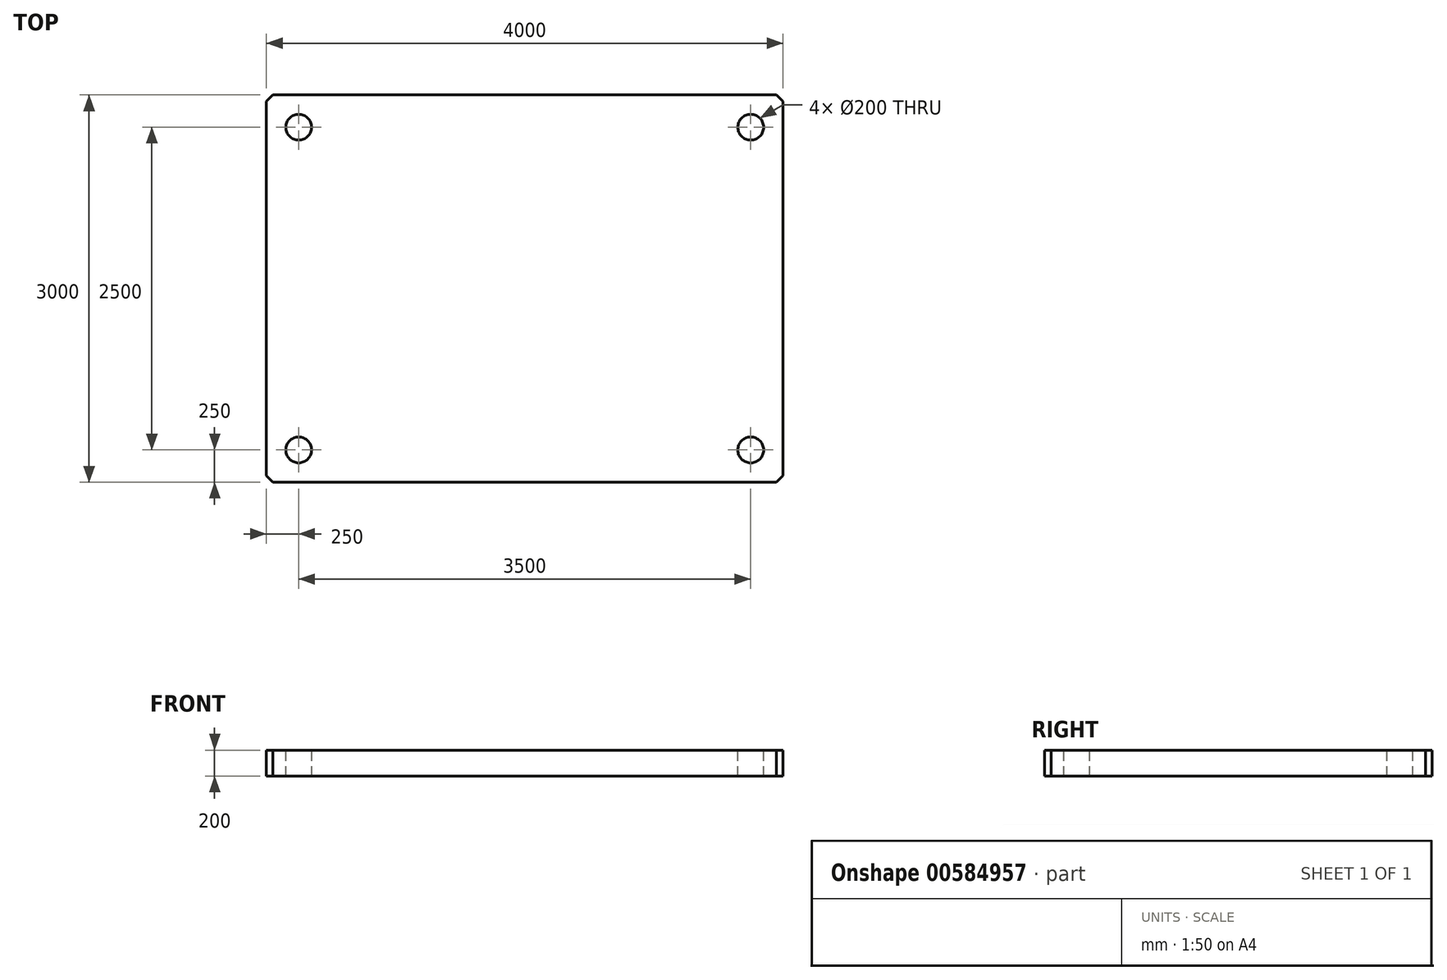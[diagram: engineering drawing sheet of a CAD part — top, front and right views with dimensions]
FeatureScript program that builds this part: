
annotation { "Feature Type Name" : "Feature", "Feature Type Description" : "" }
export const myFeature = defineFeature(function(context is Context, id is Id, definition is map)
    precondition{}
    {
        {
            var Q0;
            Q0=qCreatedBy(makeId("Top.planeOp"),FACE);
            var sketch = newSketch(context, id + "F0", { "sketchPlane" : qUnion([Q0])});
            skLineSegment(sketch, "E0.bottom", {"start": v(2000, -1500) * mm, "end": v(-2000, -1500) * mm});
            skLineSegment(sketch, "E0.top", {"start": v(2000, 1500) * mm, "end": v(-2000, 1500) * mm});
            skLineSegment(sketch, "E0.left", {"start": v(2000, -1500) * mm, "end": v(2000, 1500) * mm});
            skLineSegment(sketch, "E0.right", {"start": v(-2000, -1500) * mm, "end": v(-2000, 1500) * mm});
            skPoint(sketch, "E0.middle", {"position": v(0, 0) * mm});
            skSolve(sketch);
        }
        {
            var Q0;
            Q0 = qSketchRegion(id + "F0", true);
            extrude(context, id + "F1", {"entities" : qUnion([Q0]), "oppositeDirection" : true, "depth" : 200 * mm, "offsetDistance" : 25 * mm, "symmetric" : true});
        }
        {
            var Q0;
            Q0=makeQuery(id+"F1.opExtrude","SWEPT_EDGE",EDGE,{"disambiguationData":[OSD([sQuery(id+"F0.wireOp",EDGE,"E0.bottom"),sQuery(id+"F0.wireOp",EDGE,"E0.right")])]});
            var Q1;
            Q1=makeQuery(id+"F1.opExtrude","SWEPT_EDGE",EDGE,{"disambiguationData":[OSD([sQuery(id+"F0.wireOp",EDGE,"E0.top"),sQuery(id+"F0.wireOp",EDGE,"E0.left")])]});
            var Q2;
            Q2=makeQuery(id+"F1.opExtrude","SWEPT_EDGE",EDGE,{"disambiguationData":[OSD([sQuery(id+"F0.wireOp",EDGE,"E0.bottom"),sQuery(id+"F0.wireOp",EDGE,"E0.left")])]});
            var Q3;
            Q3=makeQuery(id+"F1.opExtrude","SWEPT_EDGE",EDGE,{"disambiguationData":[OSD([sQuery(id+"F0.wireOp",EDGE,"E0.top"),sQuery(id+"F0.wireOp",EDGE,"E0.right")])]});
            chamfer(context, id + "F2", {"entities" : qUnion([Q0, Q1, Q2, Q3]), "width" : 50 * mm, "tangentPropagation" : true});
        }
        {
            var Q0;
            Q0=makeQuery(id+"F1.opExtrude","CAP_FACE",FACE,{"disambiguationData":[OSD([sQuery(id+"F0.wireOp",EDGE,"E0.bottom"),sQuery(id+"F0.wireOp",EDGE,"E0.top"),sQuery(id+"F0.wireOp",EDGE,"E0.left"),sQuery(id+"F0.wireOp",EDGE,"E0.right")])],"isStart":true});
            var sketch = newSketch(context, id + "F3", { "sketchPlane" : qUnion([Q0])});
            skLineSegment(sketch, "E1.bottom", {"start": v(-1750, 1250) * mm, "end": v(1750, 1250) * mm, "construction": true});
            skLineSegment(sketch, "E1.top", {"start": v(-1750, -1250) * mm, "end": v(1750, -1250) * mm, "construction": true});
            skLineSegment(sketch, "E1.left", {"start": v(-1750, 1250) * mm, "end": v(-1750, -1250) * mm, "construction": true});
            skLineSegment(sketch, "E1.right", {"start": v(1750, 1250) * mm, "end": v(1750, -1250) * mm, "construction": true});
            skLineSegment(sketch, "E2", {"start": v(2000, 0) * mm, "end": v(1750, 0) * mm, "construction": true});
            skLineSegment(sketch, "E3", {"start": v(1750, 0) * mm, "end": v(1750, 0) * mm});
            skLineSegment(sketch, "E4", {"start": v(0, 1500) * mm, "end": v(0, 1250) * mm, "construction": true});
            skPoint(sketch, "E5", {"position": v(0, 1250) * mm});
            skSolve(sketch);
        }
        {
            var Q0;
            Q0=sQuery(id+"F3.wireOp",VERTEX,"E1.bottom.start");
            var Q1;
            Q1=sQuery(id+"F3.wireOp",VERTEX,"E1.right.start");
            var Q2;
            Q2=sQuery(id+"F3.wireOp",VERTEX,"E1.top.start");
            var Q3;
            Q3=sQuery(id+"F3.wireOp",VERTEX,"E1.right.end");
            var Q4;
            Q4=makeQuery(id+"F1.opExtrude","SWEPT_BODY",BODY,{"disambiguationData":[OSD([sQuery(id+"F0.wireOp",EDGE,"E0.bottom"),sQuery(id+"F0.wireOp",EDGE,"E0.top"),sQuery(id+"F0.wireOp",EDGE,"E0.left"),sQuery(id+"F0.wireOp",EDGE,"E0.right")])]});
            hole(context, id + "F4", {"style" : HoleStyle.SIMPLE, "endStyle" : HoleEndStyle.THROUGH, "holeDiameter" : 200 * mm, "majorDiameter" : 5 * mm, "isTappedThrough" : true, "tappedDepth" : 12 * mm, "tapClearance" : 3, "locations" : qUnion([Q0, Q1, Q2, Q3]), "scope" : qUnion([Q4])});
        }
    });
